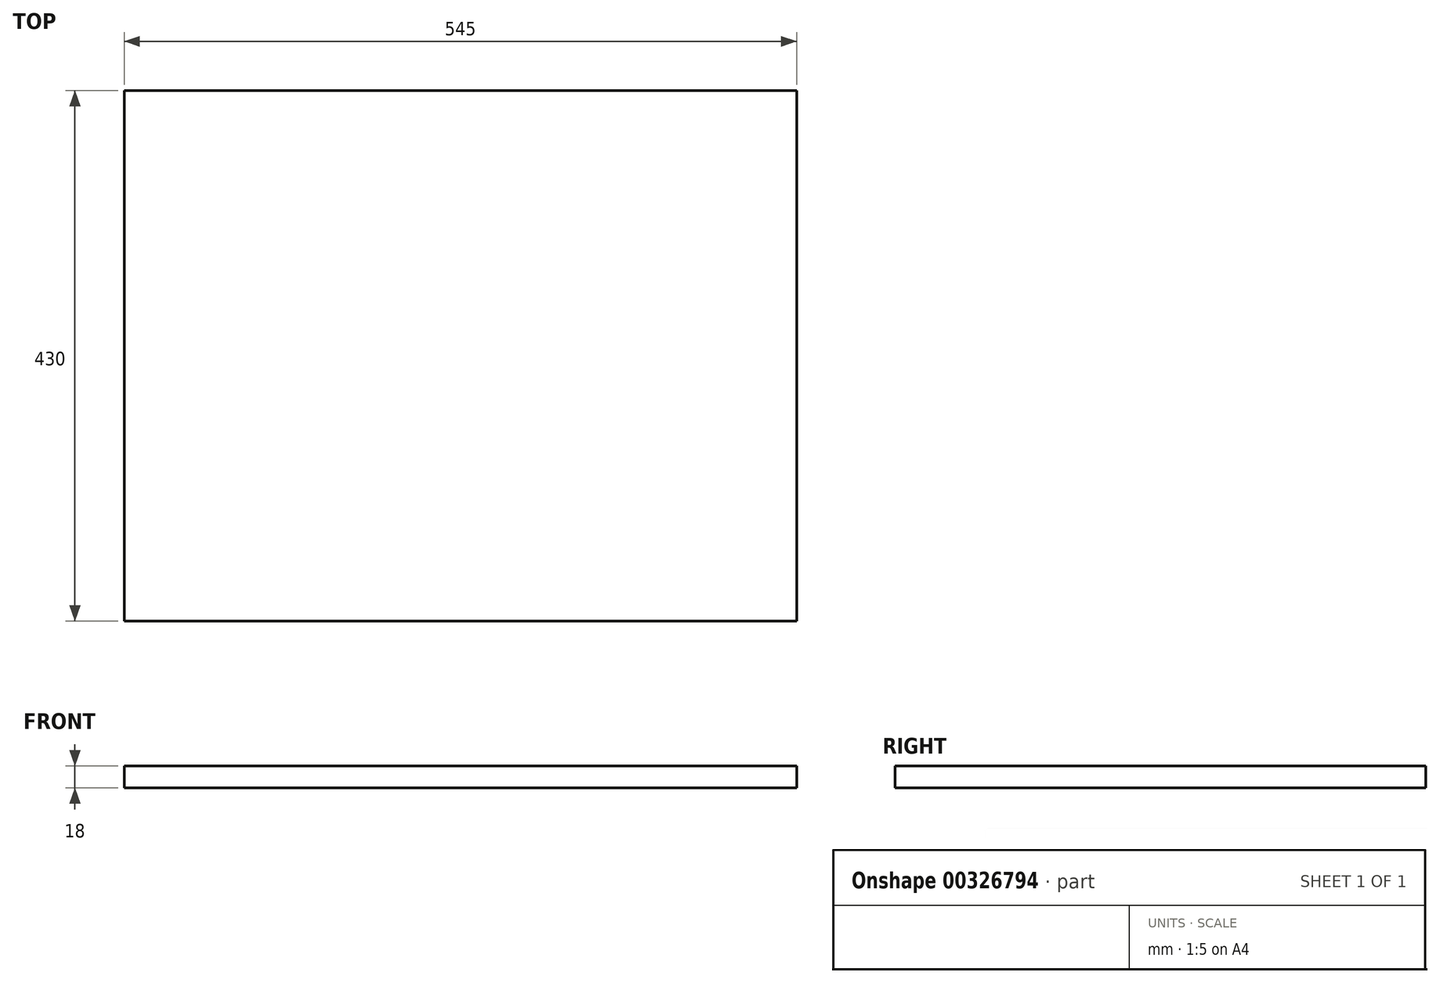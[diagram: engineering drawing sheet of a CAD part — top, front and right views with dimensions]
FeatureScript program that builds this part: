
annotation { "Feature Type Name" : "Feature", "Feature Type Description" : "" }
export const myFeature = defineFeature(function(context is Context, id is Id, definition is map)
    precondition{}
    {
        {
            var Q0;
            Q0=qCreatedBy(makeId("Top.planeOp"),FACE);
            var sketch = newSketch(context, id + "F0", { "sketchPlane" : qUnion([Q0])});
            skLineSegment(sketch, "E0.bottom", {"start": v(0, 0) * mm, "end": v(545, 0) * mm});
            skLineSegment(sketch, "E0.top", {"start": v(0, 430) * mm, "end": v(545, 430) * mm});
            skLineSegment(sketch, "E0.left", {"start": v(0, 0) * mm, "end": v(0, 430) * mm});
            skLineSegment(sketch, "E0.right", {"start": v(545, 0) * mm, "end": v(545, 430) * mm});
            skSolve(sketch);
        }
        {
            var Q0;
            Q0=qSketchRegion(id+"F0",true);
            extrude(context, id + "F1", {"entities" : qUnion([Q0]), "depth" : 18 * mm});
        }
    });
